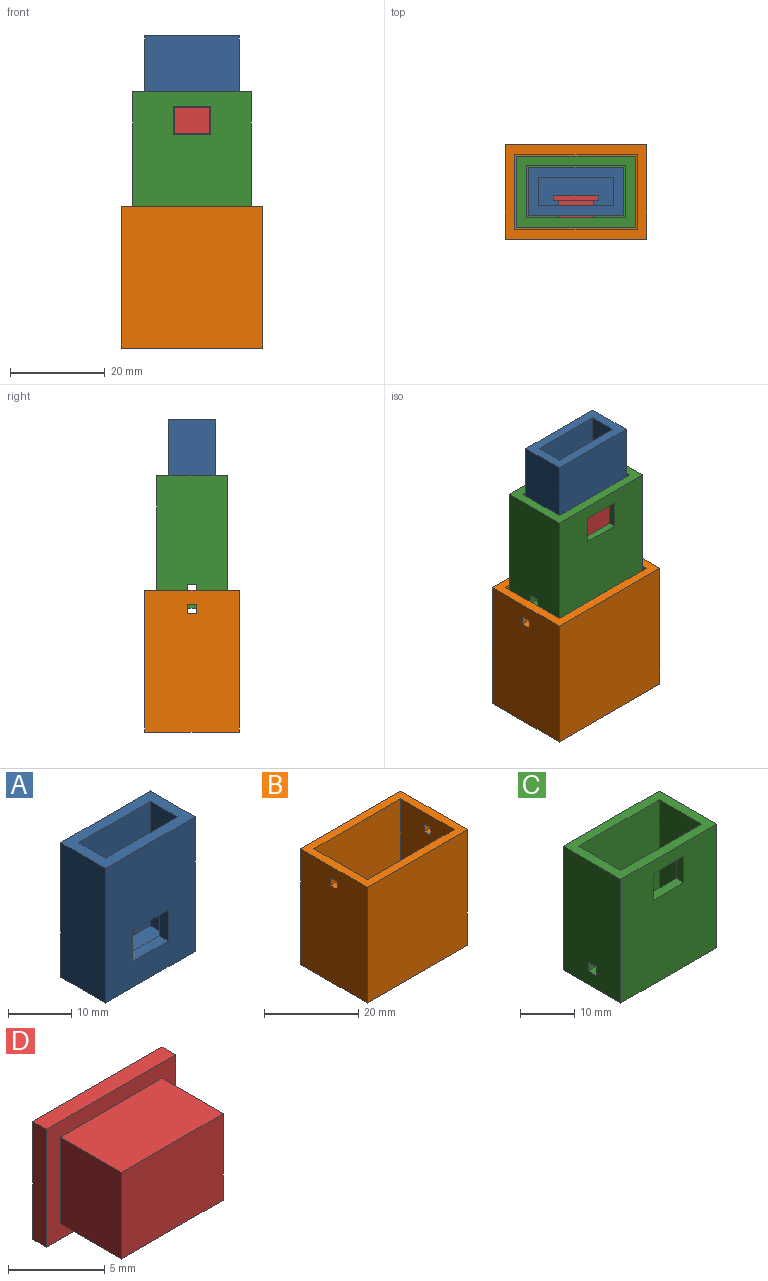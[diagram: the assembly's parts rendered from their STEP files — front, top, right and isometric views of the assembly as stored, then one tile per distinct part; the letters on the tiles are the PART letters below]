
ASSEMBLY  parts=4 mates=3
PART A: 15 faces, bbox 20x10x26 mm
  f0: plane 26x20mm, normal (0,-1,0), area 472mm2, adj f2,f4,f5,f6,f11,f12,f13,f14
  f1: plane 24x16mm, normal (0,1,0), area 336mm2, adj f2,f8,f9,f10,f11,f12,f13,f14
  f2: plane 20x10mm, normal (0,0,1), area 104mm2, adj f0,f1,f3,f4,f5,f7,f8,f9
  f3: plane 26x20mm, normal (0,1,0), area 520mm2, adj f2,f4,f5,f6
  f4: plane 26x10mm, normal (-1,0,0), area 260mm2, adj f0,f2,f3,f6
  f5: plane 26x10mm, normal (1,0,0), area 260mm2, adj f0,f2,f3,f6
  f6: plane 20x10mm, normal (0,0,-1), area 200mm2, adj f0,f3,f4,f5
  f7: plane 24x16mm, normal (0,-1,0), area 384mm2, adj f2,f8,f9,f10
  f8: plane 24x6mm, normal (1,0,0), area 144mm2, adj f1,f2,f7,f10
  f9: plane 24x6mm, normal (-1,0,0), area 144mm2, adj f1,f2,f7,f10
  f10: plane 16x6mm, normal (0,0,1), area 96mm2, adj f1,f7,f8,f9
  f11: plane 8x2mm, normal (0,0,-1), area 16mm2, adj f0,f1,f12,f14
  f12: plane 6x2mm, normal (1,0,0), area 12mm2, adj f0,f1,f11,f13
  f13: plane 8x2mm, normal (0,0,1), area 16mm2, adj f0,f1,f12,f14
  f14: plane 6x2mm, normal (-1,0,0), area 12mm2, adj f0,f1,f11,f13
PART B: 19 faces, bbox 30x20x30 mm
  f0: plane 30x20mm, normal (-1,0,0), area 596mm2, adj f4,f5,f6,f7,f15,f16,f17,f18
  f1: plane 30x20mm, normal (1,0,0), area 596mm2, adj f4,f5,f6,f7,f11,f12,f13,f14
  f2: plane 28x16mm, normal (1,0,0), area 444mm2, adj f4,f8,f9,f10,f15,f16,f17,f18
  f3: plane 28x16mm, normal (-1,0,0), area 444mm2, adj f4,f8,f9,f10,f11,f12,f13,f14
  f4: plane 30x20mm, normal (0,0,1), area 184mm2, adj f0,f1,f2,f3,f5,f6,f8,f9
  f5: plane 30x30mm, normal (0,1,0), area 900mm2, adj f0,f1,f4,f7
  f6: plane 30x30mm, normal (0,-1,0), area 900mm2, adj f0,f1,f4,f7
  f7: plane 30x20mm, normal (0,0,-1), area 600mm2, adj f0,f1,f5,f6
  f8: plane 28x26mm, normal (0,-1,0), area 728mm2, adj f2,f3,f4,f10
  f9: plane 28x26mm, normal (0,1,0), area 728mm2, adj f2,f3,f4,f10
  f10: plane 26x16mm, normal (0,0,1), area 416mm2, adj f2,f3,f8,f9
  f11: plane 2x2mm, normal (0,-1,0), area 4mm2, adj f1,f3,f12,f14
  f12: plane 2x2mm, normal (0,0,1), area 4mm2, adj f1,f3,f11,f13
  f13: plane 2x2mm, normal (0,1,0), area 4mm2, adj f1,f3,f12,f14
  f14: plane 2x2mm, normal (0,0,-1), area 4mm2, adj f1,f3,f11,f13
  f15: plane 2x2mm, normal (0,0,-1), area 4mm2, adj f0,f2,f16,f18
  f16: plane 2x2mm, normal (0,1,0), area 4mm2, adj f0,f2,f15,f17
  f17: plane 2x2mm, normal (0,0,1), area 4mm2, adj f0,f2,f16,f18
  f18: plane 2x2mm, normal (0,-1,0), area 4mm2, adj f0,f2,f15,f17
PART C: 23 faces, bbox 25x15x28 mm
  f0: plane 28x25mm, normal (0,-1,0), area 652mm2, adj f2,f3,f6,f8,f19,f20,f21,f22
  f1: plane 26x21mm, normal (0,1,0), area 498mm2, adj f4,f5,f6,f10,f19,f20,f21,f22
  f2: plane 28x15mm, normal (-1,0,0), area 416mm2, adj f0,f6,f7,f8,f15,f16,f17,f18
  f3: plane 28x15mm, normal (1,0,0), area 416mm2, adj f0,f6,f7,f8,f11,f12,f13,f14
  f4: plane 26x11mm, normal (1,0,0), area 282mm2, adj f1,f6,f9,f10,f15,f16,f17,f18
  f5: plane 26x11mm, normal (-1,0,0), area 282mm2, adj f1,f6,f9,f10,f11,f12,f13,f14
  f6: plane 25x15mm, normal (0,0,1), area 144mm2, adj f0,f1,f2,f3,f4,f5,f7,f9
  f7: plane 28x25mm, normal (0,1,0), area 700mm2, adj f2,f3,f6,f8
  f8: plane 25x15mm, normal (0,0,-1), area 375mm2, adj f0,f2,f3,f7
  f9: plane 26x21mm, normal (0,-1,0), area 546mm2, adj f4,f5,f6,f10
  f10: plane 21x11mm, normal (0,0,1), area 231mm2, adj f1,f4,f5,f9
  f11: plane 2x2mm, normal (0,-1,0), area 4mm2, adj f3,f5,f12,f14
  f12: plane 2x2mm, normal (0,0,1), area 4mm2, adj f3,f5,f11,f13
  f13: plane 2x2mm, normal (0,1,0), area 4mm2, adj f3,f5,f12,f14
  f14: plane 2x2mm, normal (0,0,-1), area 4mm2, adj f3,f5,f11,f13
  f15: plane 2x2mm, normal (0,0,-1), area 4mm2, adj f2,f4,f16,f18
  f16: plane 2x2mm, normal (0,1,0), area 4mm2, adj f2,f4,f15,f17
  f17: plane 2x2mm, normal (0,0,1), area 4mm2, adj f2,f4,f16,f18
  f18: plane 2x2mm, normal (0,-1,0), area 4mm2, adj f2,f4,f15,f17
  f19: plane 8x2mm, normal (0,0,-1), area 16mm2, adj f0,f1,f20,f22
  f20: plane 6x2mm, normal (1,0,0), area 12mm2, adj f0,f1,f19,f21
  f21: plane 8x2mm, normal (0,0,1), area 16mm2, adj f0,f1,f20,f22
  f22: plane 6x2mm, normal (-1,0,0), area 12mm2, adj f0,f1,f19,f21
PART D: 11 faces, bbox 9.5x5.5x7.5 mm
  f0: plane 7.5x4.5mm, normal (0,0,1), area 33.7mm2, adj f1,f3,f4,f5
  f1: plane 5.5x4.5mm, normal (-1,0,0), area 24.7mm2, adj f0,f2,f4,f5
  f2: plane 7.5x4.5mm, normal (0,0,-1), area 33.7mm2, adj f1,f3,f4,f5
  f3: plane 5.5x4.5mm, normal (1,0,0), area 24.7mm2, adj f0,f2,f4,f5
  f4: plane 7.5x5.5mm, normal (0,-1,0), area 41.3mm2, adj f0,f1,f2,f3
  f5: plane 9.5x7.5mm, normal (0,-1,0), area 30mm2, adj f0,f1,f2,f3,f6,f7,f8,f9
  f6: plane 9.5x1mm, normal (0,0,1), area 9.5mm2, adj f5,f7,f9,f10
  f7: plane 7.5x1mm, normal (1,0,0), area 7.5mm2, adj f5,f6,f8,f10
  f8: plane 9.5x1mm, normal (0,0,-1), area 9.5mm2, adj f5,f7,f9,f10
  f9: plane 7.5x1mm, normal (-1,0,0), area 7.5mm2, adj f5,f6,f8,f10
  f10: plane 9.5x7.5mm, normal (0,1,0), area 71.3mm2, adj f6,f7,f8,f9
PLACE A t=(-40.96,15.55,42.99)mm
PLACE B t=(-45.96,10.55,3)mm
PLACE C t=(-43.46,13.05,29.16)mm
PLACE D t=(-40.71,9.06,43.41)mm
MATE slider A.f6 <-> C.f10  axis (0,0,-1) through (-46.64,10.9,42.99)mm
MATE slider D.f10 <-> C.f0  axis (0,1,0) through (-46.64,10.06,51.16)mm
MATE slider C.f8 <-> B.f10  axis (0,0,-1) through (-46.64,10.9,29.16)mm
